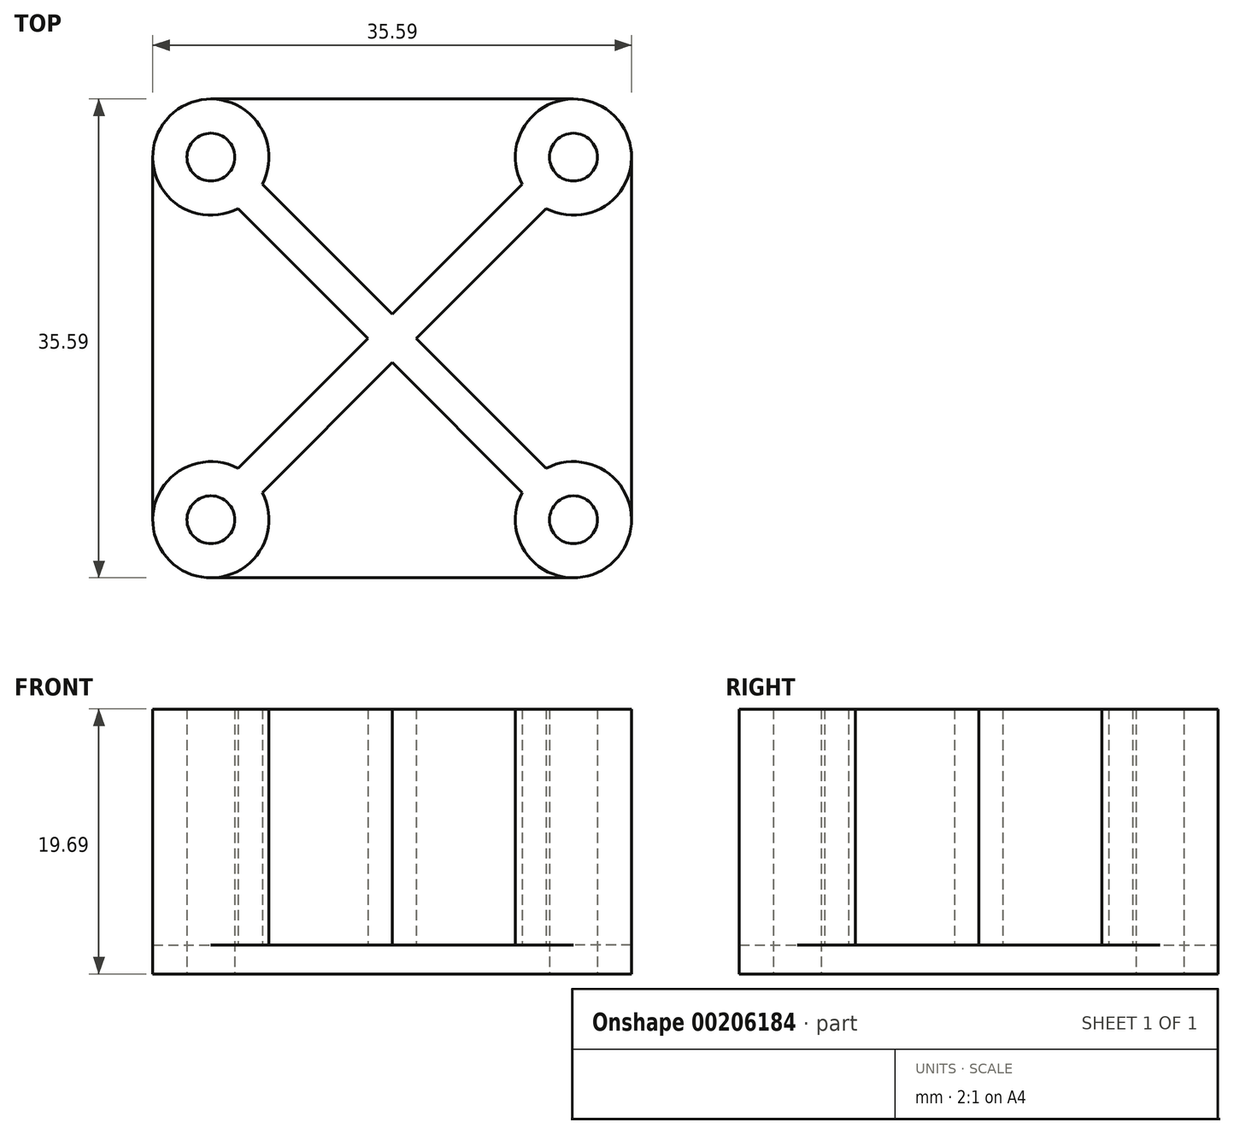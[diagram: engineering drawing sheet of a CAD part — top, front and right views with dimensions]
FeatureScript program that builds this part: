
annotation { "Feature Type Name" : "Feature", "Feature Type Description" : "" }
export const myFeature = defineFeature(function(context is Context, id is Id, definition is map)
    precondition{}
    {
        {
            var Q0;
            Q0=qCreatedBy(makeId("Top.planeOp"),FACE);
            var sketch = newSketch(context, id + "F0", { "sketchPlane" : qUnion([Q0])});
            skCircle(sketch, "E0", {"center": v(-12.14, 18.82) * mm, "radius": 1.78 * mm});
            skCircle(sketch, "E1", {"center": v(14.8, 18.82) * mm, "radius": 1.78 * mm});
            skCircle(sketch, "E2", {"center": v(14.8, -8.13) * mm, "radius": 1.78 * mm});
            skCircle(sketch, "E3", {"center": v(-12.14, -8.13) * mm, "radius": 1.78 * mm});
            skLineSegment(sketch, "E4.bottom", {"start": v(-16.46, 23.14) * mm, "end": v(19.13, 23.14) * mm});
            skLineSegment(sketch, "E4.top", {"start": v(-16.46, -12.45) * mm, "end": v(19.13, -12.45) * mm});
            skLineSegment(sketch, "E4.left", {"start": v(-16.46, 23.14) * mm, "end": v(-16.46, -12.45) * mm});
            skLineSegment(sketch, "E4.right", {"start": v(19.13, 23.14) * mm, "end": v(19.13, -12.45) * mm});
            skCircle(sketch, "E5", {"center": v(-12.14, 18.82) * mm, "radius": 4.32 * mm});
            skCircle(sketch, "E6", {"center": v(14.8, 18.82) * mm, "radius": 4.32 * mm});
            skCircle(sketch, "E7", {"center": v(14.8, -8.13) * mm, "radius": 4.32 * mm});
            skCircle(sketch, "E8", {"center": v(-12.14, -8.13) * mm, "radius": 4.32 * mm});
            skLineSegment(sketch, "E9", {"start": v(-12.14, 18.82) * mm, "end": v(14.8, -8.13) * mm, "construction": true});
            skLineSegment(sketch, "E10", {"start": v(-12.14, -8.13) * mm, "end": v(14.8, 18.82) * mm, "construction": true});
            skLineSegment(sketch, "E11", {"start": v(-8.33, 16.8) * mm, "end": v(12.79, -4.31) * mm});
            skLineSegment(sketch, "E12", {"start": v(-10.12, 15) * mm, "end": v(11, -6.1) * mm});
            skLineSegment(sketch, "E13", {"start": v(-8.33, -6.1) * mm, "end": v(12.79, 15) * mm});
            skLineSegment(sketch, "E14", {"start": v(-10.12, -4.31) * mm, "end": v(11, 16.8) * mm});
            skSolve(sketch);
        }
        {
            var Q0;
            Q0=makeQuery(id+"F0.imprint","IMPRINT",FACE,{"disambiguationData":[TD([[makeQuery(id+"F0.imprint","IMPRINT",EDGE,{"derivedFrom":sQuery(id+"F0.wireOp",EDGE,"E0")}),-1.0]])]});
            var Q1;
            Q1=makeQuery(id+"F0.imprint","IMPRINT",FACE,{"disambiguationData":[TD([[makeQuery(id+"F0.imprint","IMPRINT",EDGE,{"derivedFrom":sQuery(id+"F0.wireOp",EDGE,"E1")}),-1.0]])]});
            var Q2;
            Q2=makeQuery(id+"F0.imprint","IMPRINT",FACE,{"disambiguationData":[TD([[makeQuery(id+"F0.imprint","IMPRINT",EDGE,{"derivedFrom":sQuery(id+"F0.wireOp",EDGE,"E2")}),-1.0]])]});
            var Q3;
            Q3=makeQuery(id+"F0.imprint","IMPRINT",FACE,{"disambiguationData":[TD([[makeQuery(id+"F0.imprint","IMPRINT",EDGE,{"derivedFrom":sQuery(id+"F0.wireOp",EDGE,"E3")}),-1.0]])]});
            var Q4;
            {var subQ5=sQuery(id+"F0.wireOp",EDGE,"E5");var subQ13=sQuery(id+"F0.wireOp",EDGE,"E4.bottom");var subQ14=makeQuery(id+"F0.imprint","INTERSECT",VERTEX,{"derivedFrom":[subQ13,subQ5]});Q4=makeQuery(id+"F0.imprint","IMPRINT",FACE,{"disambiguationData":[TD([[makeQuery(id+"F0.imprint","IMPRINT",EDGE,{"disambiguationData":[TD([[subQ14,-1.0]])],"derivedFrom":subQ13}),-1.0]])]});}
            var Q5;
            {var subQ1=sQuery(id+"F0.wireOp",EDGE,"E5");var subQ7=sQuery(id+"F0.wireOp",EDGE,"E4.left");var subQ9=makeQuery(id+"F0.imprint","INTERSECT",VERTEX,{"derivedFrom":[subQ7,subQ1]});Q5=makeQuery(id+"F0.imprint","IMPRINT",FACE,{"disambiguationData":[TD([[makeQuery(id+"F0.imprint","IMPRINT",EDGE,{"disambiguationData":[TD([[subQ9,-1.0]])],"derivedFrom":subQ7}),1.0]])]});}
            var Q6;
            {var subQ5=sQuery(id+"F0.wireOp",EDGE,"E8");var subQ7=sQuery(id+"F0.wireOp",EDGE,"E4.top");var subQ8=makeQuery(id+"F0.imprint","INTERSECT",VERTEX,{"derivedFrom":[subQ7,subQ5]});Q6=makeQuery(id+"F0.imprint","IMPRINT",FACE,{"disambiguationData":[TD([[makeQuery(id+"F0.imprint","IMPRINT",EDGE,{"disambiguationData":[TD([[subQ8,-1.0]])],"derivedFrom":subQ7}),1.0]])]});}
            var Q7;
            {var subQ5=sQuery(id+"F0.wireOp",EDGE,"E4.right");var subQ7=sQuery(id+"F0.wireOp",EDGE,"E6");var subQ9=makeQuery(id+"F0.imprint","INTERSECT",VERTEX,{"derivedFrom":[subQ5,subQ7]});Q7=makeQuery(id+"F0.imprint","IMPRINT",FACE,{"disambiguationData":[TD([[makeQuery(id+"F0.imprint","IMPRINT",EDGE,{"disambiguationData":[TD([[subQ9,-1.0]])],"derivedFrom":subQ5}),-1.0]])]});}
            var Q8;
            {var subQ0=sQuery(id+"F0.wireOp",EDGE,"E11");var subQ1=sQuery(id+"F0.wireOp",EDGE,"E7");var subQ2=makeQuery(id+"F0.imprint","INTERSECT",VERTEX,{"derivedFrom":[subQ1,subQ0]});Q8=makeQuery(id+"F0.imprint","IMPRINT",FACE,{"disambiguationData":[TD([[makeQuery(id+"F0.imprint","IMPRINT",EDGE,{"disambiguationData":[TD([[subQ2,-1.0]])],"derivedFrom":subQ1}),-1.0]])]});}
            var Q9;
            {var subQ0=sQuery(id+"F0.wireOp",EDGE,"E11");var subQ1=sQuery(id+"F0.wireOp",EDGE,"E5");var subQ2=makeQuery(id+"F0.imprint","INTERSECT",VERTEX,{"derivedFrom":[subQ1,subQ0]});Q9=makeQuery(id+"F0.imprint","IMPRINT",FACE,{"disambiguationData":[TD([[makeQuery(id+"F0.imprint","IMPRINT",EDGE,{"disambiguationData":[TD([[subQ2,1.0]])],"derivedFrom":subQ1}),-1.0]])]});}
            var Q10;
            {var subQ0=sQuery(id+"F0.wireOp",EDGE,"E13");var subQ1=sQuery(id+"F0.wireOp",EDGE,"E6");var subQ2=makeQuery(id+"F0.imprint","INTERSECT",VERTEX,{"derivedFrom":[subQ1,subQ0]});Q10=makeQuery(id+"F0.imprint","IMPRINT",FACE,{"disambiguationData":[TD([[makeQuery(id+"F0.imprint","IMPRINT",EDGE,{"disambiguationData":[TD([[subQ2,1.0]])],"derivedFrom":subQ1}),-1.0]])]});}
            var Q11;
            {var subQ0=sQuery(id+"F0.wireOp",EDGE,"E13");var subQ1=sQuery(id+"F0.wireOp",EDGE,"E8");var subQ2=makeQuery(id+"F0.imprint","INTERSECT",VERTEX,{"derivedFrom":[subQ1,subQ0]});Q11=makeQuery(id+"F0.imprint","IMPRINT",FACE,{"disambiguationData":[TD([[makeQuery(id+"F0.imprint","IMPRINT",EDGE,{"disambiguationData":[TD([[subQ2,-1.0]])],"derivedFrom":subQ1}),-1.0]])]});}
            var Q12;
            {var subQ0=sQuery(id+"F0.wireOp",EDGE,"E14");var subQ1=sQuery(id+"F0.wireOp",EDGE,"E11");var subQ2=makeQuery(id+"F0.imprint","INTERSECT",VERTEX,{"derivedFrom":[subQ1,subQ0]});Q12=makeQuery(id+"F0.imprint","IMPRINT",FACE,{"disambiguationData":[TD([[makeQuery(id+"F0.imprint","IMPRINT",EDGE,{"disambiguationData":[TD([[subQ2,-1.0]])],"derivedFrom":subQ1}),-1.0]])]});}
            extrude(context, id + "F1", {"entities" : qUnion([Q0, Q1, Q2, Q3, Q4, Q5, Q6, Q7, Q8, Q9, Q10, Q11, Q12]), "depth" : 2.16 * mm});
        }
        {
            var Q0;
            Q0=makeQuery(id+"F0.imprint","IMPRINT",FACE,{"disambiguationData":[TD([[makeQuery(id+"F0.imprint","IMPRINT",EDGE,{"derivedFrom":sQuery(id+"F0.wireOp",EDGE,"E0")}),-1.0]])]});
            var Q1;
            Q1=makeQuery(id+"F0.imprint","IMPRINT",FACE,{"disambiguationData":[TD([[makeQuery(id+"F0.imprint","IMPRINT",EDGE,{"derivedFrom":sQuery(id+"F0.wireOp",EDGE,"E1")}),-1.0]])]});
            var Q2;
            Q2=makeQuery(id+"F0.imprint","IMPRINT",FACE,{"disambiguationData":[TD([[makeQuery(id+"F0.imprint","IMPRINT",EDGE,{"derivedFrom":sQuery(id+"F0.wireOp",EDGE,"E2")}),-1.0]])]});
            var Q3;
            Q3=makeQuery(id+"F0.imprint","IMPRINT",FACE,{"disambiguationData":[TD([[makeQuery(id+"F0.imprint","IMPRINT",EDGE,{"derivedFrom":sQuery(id+"F0.wireOp",EDGE,"E3")}),-1.0]])]});
            var Q4;
            {var subQ0=sQuery(id+"F0.wireOp",EDGE,"E11");var subQ1=sQuery(id+"F0.wireOp",EDGE,"E7");var subQ2=makeQuery(id+"F0.imprint","INTERSECT",VERTEX,{"derivedFrom":[subQ1,subQ0]});Q4=makeQuery(id+"F0.imprint","IMPRINT",FACE,{"disambiguationData":[TD([[makeQuery(id+"F0.imprint","IMPRINT",EDGE,{"disambiguationData":[TD([[subQ2,-1.0]])],"derivedFrom":subQ1}),-1.0]])]});}
            var Q5;
            {var subQ0=sQuery(id+"F0.wireOp",EDGE,"E13");var subQ1=sQuery(id+"F0.wireOp",EDGE,"E8");var subQ2=makeQuery(id+"F0.imprint","INTERSECT",VERTEX,{"derivedFrom":[subQ1,subQ0]});Q5=makeQuery(id+"F0.imprint","IMPRINT",FACE,{"disambiguationData":[TD([[makeQuery(id+"F0.imprint","IMPRINT",EDGE,{"disambiguationData":[TD([[subQ2,-1.0]])],"derivedFrom":subQ1}),-1.0]])]});}
            var Q6;
            {var subQ0=sQuery(id+"F0.wireOp",EDGE,"E11");var subQ1=sQuery(id+"F0.wireOp",EDGE,"E5");var subQ2=makeQuery(id+"F0.imprint","INTERSECT",VERTEX,{"derivedFrom":[subQ1,subQ0]});Q6=makeQuery(id+"F0.imprint","IMPRINT",FACE,{"disambiguationData":[TD([[makeQuery(id+"F0.imprint","IMPRINT",EDGE,{"disambiguationData":[TD([[subQ2,1.0]])],"derivedFrom":subQ1}),-1.0]])]});}
            var Q7;
            {var subQ0=sQuery(id+"F0.wireOp",EDGE,"E14");var subQ1=sQuery(id+"F0.wireOp",EDGE,"E11");var subQ2=makeQuery(id+"F0.imprint","INTERSECT",VERTEX,{"derivedFrom":[subQ1,subQ0]});Q7=makeQuery(id+"F0.imprint","IMPRINT",FACE,{"disambiguationData":[TD([[makeQuery(id+"F0.imprint","IMPRINT",EDGE,{"disambiguationData":[TD([[subQ2,-1.0]])],"derivedFrom":subQ1}),-1.0]])]});}
            var Q8;
            {var subQ0=sQuery(id+"F0.wireOp",EDGE,"E13");var subQ1=sQuery(id+"F0.wireOp",EDGE,"E6");var subQ2=makeQuery(id+"F0.imprint","INTERSECT",VERTEX,{"derivedFrom":[subQ1,subQ0]});Q8=makeQuery(id+"F0.imprint","IMPRINT",FACE,{"disambiguationData":[TD([[makeQuery(id+"F0.imprint","IMPRINT",EDGE,{"disambiguationData":[TD([[subQ2,1.0]])],"derivedFrom":subQ1}),-1.0]])]});}
            extrude(context, id + "F2", {"entities" : qUnion([Q0, Q1, Q2, Q3, Q4, Q5, Q6, Q7, Q8]), "operationType" : NewBodyOperationType.ADD, "depth" : 19.68 * mm});
        }
    });
